# Revit family: IS_ConnectBlue_Multiproduct_BIM_DE_A5801;A5802;A6006
name_source: partatom
category: Plumbing Fixtures
revit_build: Autodesk Revit MEP 2014 (Build: 20130308_1515(x64)
units: mm (PartAtom-declared; Revit-internal decimal feet)

## types (3) — shared parameters
Accessories = www.idealstandard.de\ersatzteile
AreaUnits = millimeters
Assembly Code = C1030200
AssetType = Fixed
Brand = Ideal Standard
CodePerformance = EN 817, DIN 4109
Color = Chrome
ConnectionType = Plumbing
DurationUnit = year
ExpectedLife = 25
FaucetFunction = MIXED
FaucetOperation = LEVERHANDLE
FaucetType = PILLAR
Finish = chrome
FlowRate = 26/24 Liters @ 3bar
IfcExportAs = IfcValveType
IfcExportType = FAUCET
InstallationInstructions = www.idealstandard.de/produkte
LinearUnits = millimeters
ManufacturerURL = www.idealstandard.de
Material = Brass
NBSDescription = Shower mixers
NBSReference = 45-35-70/335
NominalHeight = 197 mm
NominalLength = 91 mm
NominalWidth = 163 mm
ProductInformation = www.idealstandard.de/produkte
Shape = Sculptured
Size = 172x180x215mm
Space = Internal
SpareParts = www.idealstandard.de/ersatzteile
TMV3 = Yes
TestPressure = 10 Bar
URL = www.idealstandard.com
Uniclass2015Code = Pr_40_20_87_81
Uniclass2015Title = Shower thermostatic water supply sets
Uniclass2015Version = Products v1.1
Version = 1
VolumeUnits = Litres
WarrantyDescription = Manufacturers Warranty
WarrantyDurationUnit = year
WorkingPressure = 1-5 Bar
zero-valued in all types: CWFU, Cost, Default Elevation, HWFU, WFU

## per-type parameters (varying)
| type | A5802AA | BIMObjectName | BarCode | Category | Description | Features | Model | ModelNumber | ModelReference | Name | NettWeight |
| A5801AA - Connect Blue build-in shower single lever mixer | No | ISI_IdealStandard_ShowerMixers_ConnectBlue_A5801AA | 4015413320344 | SanitaryTerminal_FAUCET | Connect Blue build-in shower single lever mixer | Connect Blue build-in shower single lever mixer | A5801AA | A5801AA | Connect Blue build-in shower single lever mixer | ShowerMixers_ConnectBlue_A5801AA_IdealStandard | 1,173 kg |
| A5802AA - Connect Blue bath shower single lever mixer | Yes | ISI_IdealStandard_ShowerMixers_ConnectBlue_A5802AA | 4015413320351 | SanitaryTerminal_FAUCET | Connect Blue bath shower single lever mixer | Connect Blue bath shower single lever mixer | A5802AA | A5802AA | Connect Blue bath shower single lever mixer | ShowerMixers_ConnectBlue_A5802AA_IdealStandard | 1,362 kg |
| A6006AA - Connect Blue build-in bath shower single lever mixer | Yes | ISI_IdealStandard_ShowerMixers_ConnectBlue_A6006AA | 4015413317498 | SanitaryTerminal_SHOWER | Connect Blue build-in bath shower single lever mixer | Connect Blue build-in bath shower single lever mixer | A6006AA | A6006AA | Connect Blue build-in bath shower single lever mixer | ShowerMixers_ConnectBlue_A6006AA_IdealStandard | 1,26 kg |

## geometry (parser evidence)
native form markers: Sweep x3
no freeform markers — native parametric forms only
